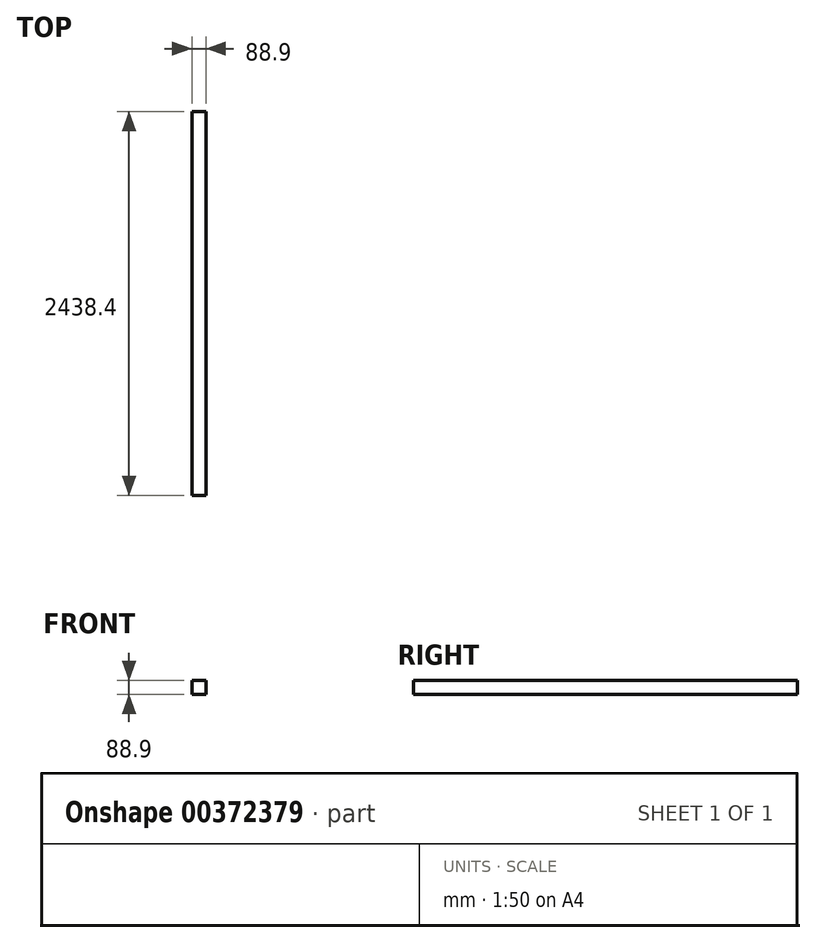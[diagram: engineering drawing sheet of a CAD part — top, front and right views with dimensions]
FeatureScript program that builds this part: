
annotation { "Feature Type Name" : "Feature", "Feature Type Description" : "" }
export const myFeature = defineFeature(function(context is Context, id is Id, definition is map)
    precondition{}
    {
        {
            var Q0;
            Q0=qCreatedBy(makeId("Front.planeOp"),FACE);
            var sketch = newSketch(context, id + "F0", { "sketchPlane" : qUnion([Q0])});
            skLineSegment(sketch, "E0.bottom", {"start": v(-44.45, 44.45) * mm, "end": v(44.45, 44.45) * mm});
            skLineSegment(sketch, "E0.top", {"start": v(-44.45, -44.45) * mm, "end": v(44.45, -44.45) * mm});
            skLineSegment(sketch, "E0.left", {"start": v(-44.45, 44.45) * mm, "end": v(-44.45, -44.45) * mm});
            skLineSegment(sketch, "E0.right", {"start": v(44.45, 44.45) * mm, "end": v(44.45, -44.45) * mm});
            skPoint(sketch, "E0.middle", {"position": v(0, 0) * mm});
            skSolve(sketch);
        }
        {
            var Q0;
            Q0=qSketchRegion(id+"F0",true);
            extrude(context, id + "F1", {"entities" : qUnion([Q0]), "endBound" : BoundingType.SYMMETRIC, "oppositeDirection" : true, "depth" : 2438.4 * mm});
        }
    });
